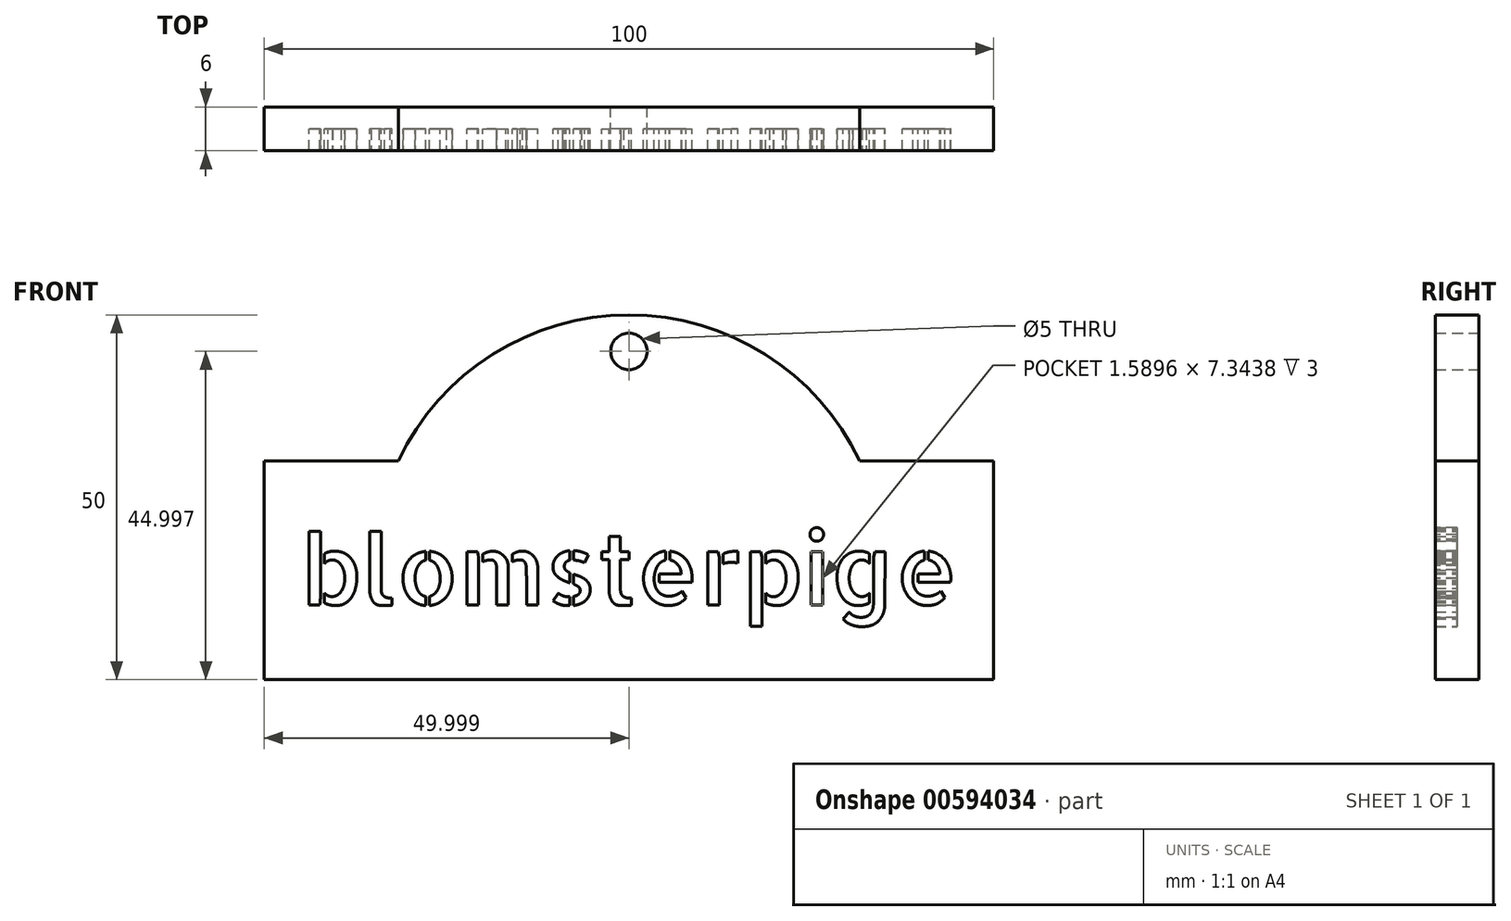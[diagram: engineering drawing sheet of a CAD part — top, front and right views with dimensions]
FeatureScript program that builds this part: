
annotation { "Feature Type Name" : "Feature", "Feature Type Description" : "" }
export const myFeature = defineFeature(function(context is Context, id is Id, definition is map)
    precondition{}
    {
        {
            var Q0;
            Q0=qCreatedBy(makeId("Front.planeOp"),FACE);
            var sketch = newSketch(context, id + "F0", { "sketchPlane" : qUnion([Q0])});
            skLineSegment(sketch, "E0.bottom", {"start": v(-100.44, 43.18) * mm, "end": v(-82.06, 43.18) * mm});
            skLineSegment(sketch, "E0.top", {"start": v(-100.44, 13.18) * mm, "end": v(-0.44, 13.18) * mm});
            skLineSegment(sketch, "E0.left", {"start": v(-100.44, 43.18) * mm, "end": v(-100.44, 13.18) * mm});
            skLineSegment(sketch, "E0.right", {"start": v(-0.44, 43.18) * mm, "end": v(-0.44, 13.18) * mm});
            skArc(sketch, "E1", {"start": v(-18.82, 43.18) * mm, "mid": v(-50.44, 63.18) * mm, "end": v(-82.06, 43.18) * mm});
            skCircle(sketch, "E2", {"center": v(-50.44, 58.18) * mm, "radius": 2.5 * mm});
            skText(sketch, "E3", { "text": "blomsterpige\n", "fontName": "AllertaStencil-Regular.ttf"});
            skPoint(sketch, "E4", {"position": v(-50.44, 13.18) * mm});
            skPoint(sketch, "E5", {"position": v(-0.44, 28.18) * mm});
            skPoint(sketch, "E6", {"position": v(-50.44, 43.18) * mm});
            skPoint(sketch, "E7", {"position": v(-50.44, 63.18) * mm});
            skPoint(sketch, "E8", {"position": v(-5.44, 28.18) * mm});
            skLineSegment(sketch, "E9.trimOffspring", {"start": v(-18.82, 43.18) * mm, "end": v(-0.44, 43.18) * mm});
            const initialGuessF0  = {"E3": [-0.09544, 0.02338, 1, 0, 0.0096]};
            skSetInitialGuess(sketch, initialGuessF0);
            skSolve(sketch);
        }
        {
            var Q0;
            Q0=makeQuery(id+"F0.imprint","IMPRINT",FACE,{"disambiguationData":[TD([[makeQuery(id+"F0.imprint","IMPRINT",EDGE,{"derivedFrom":sQuery(id+"F0.wireOp",EDGE,"E3.sketch_text.stroke-104")}),-1.0]])]});
            var Q1;
            Q1=makeQuery(id+"F0.imprint","IMPRINT",FACE,{"disambiguationData":[TD([[makeQuery(id+"F0.imprint","IMPRINT",EDGE,{"derivedFrom":sQuery(id+"F0.wireOp",EDGE,"E3.sketch_text.stroke-151")}),-1.0]])]});
            var Q2;
            Q2=makeQuery(id+"F0.imprint","IMPRINT",FACE,{"disambiguationData":[TD([[makeQuery(id+"F0.imprint","IMPRINT",EDGE,{"derivedFrom":sQuery(id+"F0.wireOp",EDGE,"E3.sketch_text.stroke-142")}),-1.0]])]});
            var Q3;
            Q3 = qSketchRegion(id + "F0", true);
            var Q4;
            Q4=makeQuery(id+"F0.imprint","IMPRINT",FACE,{"disambiguationData":[TD([[makeQuery(id+"F0.imprint","IMPRINT",EDGE,{"derivedFrom":sQuery(id+"F0.wireOp",EDGE,"E3.sketch_text.stroke-122")}),-1.0]])]});
            var Q5;
            Q5=makeQuery(id+"F0.imprint","IMPRINT",FACE,{"disambiguationData":[TD([[makeQuery(id+"F0.imprint","IMPRINT",EDGE,{"derivedFrom":sQuery(id+"F0.wireOp",EDGE,"E3.sketch_text.stroke-227")}),-1.0]])]});
            var Q6;
            Q6=makeQuery(id+"F0.imprint","IMPRINT",FACE,{"disambiguationData":[TD([[makeQuery(id+"F0.imprint","IMPRINT",EDGE,{"derivedFrom":sQuery(id+"F0.wireOp",EDGE,"E3.sketch_text.stroke-241")}),-1.0]])]});
            var Q7;
            Q7=makeQuery(id+"F0.imprint","IMPRINT",FACE,{"disambiguationData":[TD([[makeQuery(id+"F0.imprint","IMPRINT",EDGE,{"derivedFrom":sQuery(id+"F0.wireOp",EDGE,"E3.sketch_text.stroke-246")}),-1.0]])]});
            var Q8;
            Q8=makeQuery(id+"F0.imprint","IMPRINT",FACE,{"disambiguationData":[TD([[makeQuery(id+"F0.imprint","IMPRINT",EDGE,{"derivedFrom":sQuery(id+"F0.wireOp",EDGE,"E3.sketch_text.stroke-272")}),-1.0]])]});
            var Q9;
            Q9=makeQuery(id+"F0.imprint","IMPRINT",FACE,{"disambiguationData":[TD([[makeQuery(id+"F0.imprint","IMPRINT",EDGE,{"derivedFrom":sQuery(id+"F0.wireOp",EDGE,"E3.sketch_text.stroke-284")}),-1.0]])]});
            var Q10;
            Q10=makeQuery(id+"F0.imprint","IMPRINT",FACE,{"disambiguationData":[TD([[makeQuery(id+"F0.imprint","IMPRINT",EDGE,{"derivedFrom":sQuery(id+"F0.wireOp",EDGE,"E3.sketch_text.stroke-203")}),-1.0]])]});
            var Q11;
            Q11=makeQuery(id+"F0.imprint","IMPRINT",FACE,{"disambiguationData":[TD([[makeQuery(id+"F0.imprint","IMPRINT",EDGE,{"derivedFrom":sQuery(id+"F0.wireOp",EDGE,"E3.sketch_text.stroke-165")}),-1.0]])]});
            var Q12;
            Q12=makeQuery(id+"F0.imprint","IMPRINT",FACE,{"disambiguationData":[TD([[makeQuery(id+"F0.imprint","IMPRINT",EDGE,{"derivedFrom":sQuery(id+"F0.wireOp",EDGE,"E3.sketch_text.stroke-190")}),-1.0]])]});
            var Q13;
            Q13=makeQuery(id+"F0.imprint","IMPRINT",FACE,{"disambiguationData":[TD([[makeQuery(id+"F0.imprint","IMPRINT",EDGE,{"derivedFrom":sQuery(id+"F0.wireOp",EDGE,"E3.sketch_text.stroke-0")}),-1.0]])]});
            var Q14;
            Q14=makeQuery(id+"F0.imprint","IMPRINT",FACE,{"disambiguationData":[TD([[makeQuery(id+"F0.imprint","IMPRINT",EDGE,{"derivedFrom":sQuery(id+"F0.wireOp",EDGE,"E3.sketch_text.stroke-6")}),-1.0]])]});
            var Q15;
            Q15=makeQuery(id+"F0.imprint","IMPRINT",FACE,{"disambiguationData":[TD([[makeQuery(id+"F0.imprint","IMPRINT",EDGE,{"derivedFrom":sQuery(id+"F0.wireOp",EDGE,"E3.sketch_text.stroke-33")}),-1.0]])]});
            var Q16;
            Q16=makeQuery(id+"F0.imprint","IMPRINT",FACE,{"disambiguationData":[TD([[makeQuery(id+"F0.imprint","IMPRINT",EDGE,{"derivedFrom":sQuery(id+"F0.wireOp",EDGE,"E3.sketch_text.stroke-51")}),-1.0]])]});
            var Q17;
            Q17=makeQuery(id+"F0.imprint","IMPRINT",FACE,{"disambiguationData":[TD([[makeQuery(id+"F0.imprint","IMPRINT",EDGE,{"derivedFrom":sQuery(id+"F0.wireOp",EDGE,"E3.sketch_text.stroke-67")}),-1.0]])]});
            var Q18;
            Q18=makeQuery(id+"F0.imprint","IMPRINT",FACE,{"disambiguationData":[TD([[makeQuery(id+"F0.imprint","IMPRINT",EDGE,{"derivedFrom":sQuery(id+"F0.wireOp",EDGE,"E3.sketch_text.stroke-83")}),-1.0]])]});
            var Q19;
            Q19=makeQuery(id+"F0.imprint","IMPRINT",FACE,{"disambiguationData":[TD([[makeQuery(id+"F0.imprint","IMPRINT",EDGE,{"derivedFrom":sQuery(id+"F0.wireOp",EDGE,"E3.sketch_text.stroke-88")}),-1.0]])]});
            var Q20;
            Q20=makeQuery(id+"F0.imprint","IMPRINT",FACE,{"disambiguationData":[TD([[makeQuery(id+"F0.imprint","IMPRINT",EDGE,{"derivedFrom":sQuery(id+"F0.wireOp",EDGE,"E3.sketch_text.stroke-340")}),-1.0]])]});
            var Q21;
            Q21=makeQuery(id+"F0.imprint","IMPRINT",FACE,{"disambiguationData":[TD([[makeQuery(id+"F0.imprint","IMPRINT",EDGE,{"derivedFrom":sQuery(id+"F0.wireOp",EDGE,"E3.sketch_text.stroke-310")}),-1.0]])]});
            var Q22;
            Q22=makeQuery(id+"F0.imprint","IMPRINT",FACE,{"disambiguationData":[TD([[makeQuery(id+"F0.imprint","IMPRINT",EDGE,{"derivedFrom":sQuery(id+"F0.wireOp",EDGE,"E3.sketch_text.stroke-327")}),-1.0]])]});
            var Q23;
            Q23=makeQuery(id+"F0.imprint","IMPRINT",FACE,{"disambiguationData":[TD([[makeQuery(id+"F0.imprint","IMPRINT",EDGE,{"derivedFrom":sQuery(id+"F0.wireOp",EDGE,"E0.bottom")}),-1.0]])]});
            var Q24;
            Q24=makeQuery(id+"F0.imprint","IMPRINT",FACE,{"disambiguationData":[TD([[makeQuery(id+"F0.imprint","IMPRINT",EDGE,{"derivedFrom":sQuery(id+"F0.wireOp",EDGE,"E3.sketch_text.stroke-136")}),-1.0]])]});
            var Q25;
            Q25=makeQuery(id+"F0.imprint","IMPRINT",FACE,{"disambiguationData":[TD([[makeQuery(id+"F0.imprint","IMPRINT",EDGE,{"derivedFrom":sQuery(id+"F0.wireOp",EDGE,"E3.sketch_text.stroke-234")}),-1.0]])]});
            var Q26;
            Q26=makeQuery(id+"F0.imprint","IMPRINT",FACE,{"disambiguationData":[TD([[makeQuery(id+"F0.imprint","IMPRINT",EDGE,{"derivedFrom":sQuery(id+"F0.wireOp",EDGE,"E3.sketch_text.stroke-276")}),-1.0]])]});
            extrude(context, id + "F1", {"entities" : qUnion([Q0, Q1, Q2, Q3, Q4, Q5, Q6, Q7, Q8, Q9, Q10, Q11, Q12, Q13, Q14, Q15, Q16, Q17, Q18, Q19, Q20, Q21, Q22, Q23, Q24, Q25, Q26]), "depth" : 3 * mm, "offsetDistance" : 25 * mm});
        }
        {
            var Q0;
            Q0=makeQuery(id+"F0.imprint","IMPRINT",FACE,{"disambiguationData":[TD([[makeQuery(id+"F0.imprint","IMPRINT",EDGE,{"derivedFrom":sQuery(id+"F0.wireOp",EDGE,"E0.bottom")}),-1.0]])]});
            extrude(context, id + "F2", {"entities" : qUnion([Q0]), "operationType" : NewBodyOperationType.ADD, "depth" : 6 * mm, "offsetDistance" : 25 * mm});
        }
    });
